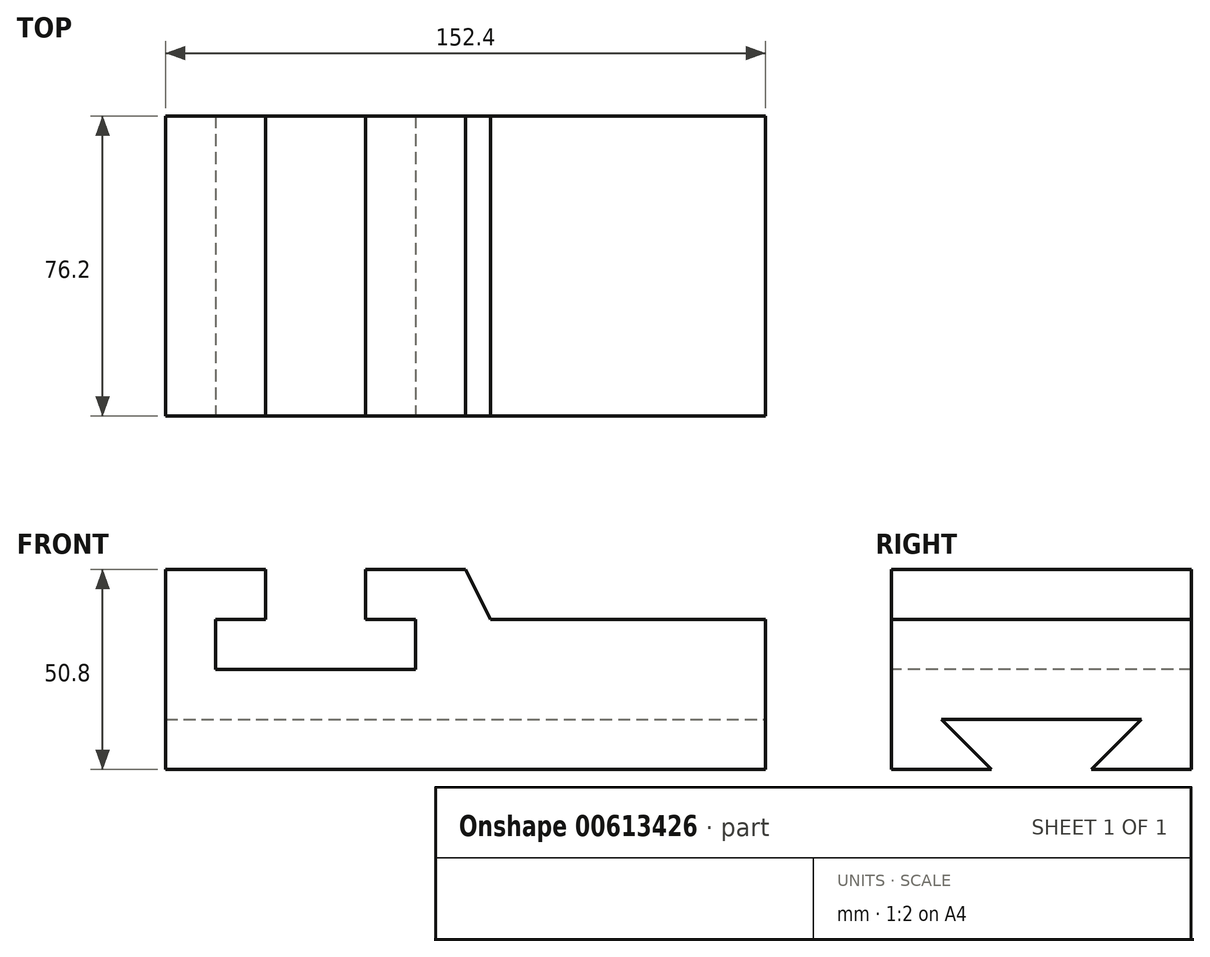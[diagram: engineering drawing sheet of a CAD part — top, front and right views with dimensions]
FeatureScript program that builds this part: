
annotation { "Feature Type Name" : "Feature", "Feature Type Description" : "" }
export const myFeature = defineFeature(function(context is Context, id is Id, definition is map)
    precondition{}
    {
        {
            var Q0;
            Q0=qCreatedBy(makeId("Front.planeOp"),FACE);
            var sketch = newSketch(context, id + "F0", { "sketchPlane" : qUnion([Q0])});
            skLineSegment(sketch, "E0.bottom", {"start": v(0, 0) * mm, "end": v(152.4, 0) * mm});
            skLineSegment(sketch, "E0.top", {"start": v(0, 50.8) * mm, "end": v(152.4, 50.8) * mm});
            skLineSegment(sketch, "E0.left", {"start": v(0, 0) * mm, "end": v(0, 50.8) * mm});
            skLineSegment(sketch, "E0.right", {"start": v(152.4, 0) * mm, "end": v(152.4, 50.8) * mm});
            skSolve(sketch);
        }
        {
            var Q0;
            Q0=makeQuery(id+"F0.imprint","IMPRINT",FACE,{"disambiguationData":[TD([[makeQuery(id+"F0.imprint","IMPRINT",EDGE,{"derivedFrom":sQuery(id+"F0.wireOp",EDGE,"E0.bottom")}),1.0]])]});
            extrude(context, id + "F1", {"entities" : qUnion([Q0]), "depth" : 76.2 * mm, "offsetDistance" : 25.4 * mm});
        }
        {
            var Q0;
            Q0=makeQuery(id+"F1.opExtrude","SWEPT_FACE",FACE,{"disambiguationData":[OSD([sQuery(id+"F0.wireOp",EDGE,"E0.right")])]});
            var sketch = newSketch(context, id + "F2", { "sketchPlane" : qUnion([Q0])});
            skLineSegment(sketch, "E1", {"start": v(-38.1, 0) * mm, "end": v(-25.4, 0) * mm});
            skLineSegment(sketch, "E2", {"start": v(-38.1, 0) * mm, "end": v(-50.8, 0) * mm});
            skLineSegment(sketch, "E3", {"start": v(-38.1, 12.7) * mm, "end": v(-12.7, 12.7) * mm});
            skLineSegment(sketch, "E4", {"start": v(-12.7, 12.7) * mm, "end": v(-25.4, 0) * mm});
            skLineSegment(sketch, "E5", {"start": v(-38.1, 12.7) * mm, "end": v(-63.5, 12.7) * mm});
            skLineSegment(sketch, "E6", {"start": v(-63.5, 12.7) * mm, "end": v(-50.8, 0) * mm});
            skSolve(sketch);
        }
        {
            var Q0;
            Q0 = qSketchRegion(id + "F2", true);
            extrude(context, id + "F3", {"entities" : qUnion([Q0]), "operationType" : NewBodyOperationType.REMOVE, "oppositeDirection" : true, "depth" : 152.4 * mm, "offsetDistance" : 25.4 * mm});
        }
        {
            var Q0;
            Q0=makeQuery(id+"F1.opExtrude","CAP_FACE",FACE,{"disambiguationData":[OSD([sQuery(id+"F0.wireOp",EDGE,"E0.bottom"),sQuery(id+"F0.wireOp",EDGE,"E0.top"),sQuery(id+"F0.wireOp",EDGE,"E0.left"),sQuery(id+"F0.wireOp",EDGE,"E0.right")])],"isStart":false});
            var sketch = newSketch(context, id + "F4", { "sketchPlane" : qUnion([Q0])});
            skLineSegment(sketch, "E7", {"start": v(0, 50.8) * mm, "end": v(25.4, 50.8) * mm});
            skLineSegment(sketch, "E8", {"start": v(25.4, 50.8) * mm, "end": v(25.4, 38.1) * mm});
            skLineSegment(sketch, "E9", {"start": v(25.4, 38.1) * mm, "end": v(12.7, 38.1) * mm});
            skLineSegment(sketch, "E10", {"start": v(12.7, 38.1) * mm, "end": v(12.7, 25.4) * mm});
            skLineSegment(sketch, "E11", {"start": v(12.7, 25.4) * mm, "end": v(63.5, 25.4) * mm});
            skLineSegment(sketch, "E12", {"start": v(63.5, 25.4) * mm, "end": v(63.5, 38.1) * mm});
            skLineSegment(sketch, "E13", {"start": v(63.5, 38.1) * mm, "end": v(50.8, 38.1) * mm});
            skLineSegment(sketch, "E14", {"start": v(50.8, 38.1) * mm, "end": v(50.8, 50.8) * mm});
            skSolve(sketch);
        }
        {
            var Q0;
            Q0 = qSketchRegion(id + "F4", true);
            var Q1;
            {var subQ0=sQuery(id+"F4.wireOp",EDGE,"E8");Q1=makeQuery(id+"F4.imprint","IMPRINT",FACE,{"disambiguationData":[TD([[makeQuery(id+"F4.imprint","IMPRINT",EDGE,{"derivedFrom":subQ0}),1.0]])]});}
            extrude(context, id + "F5", {"entities" : qUnion([Q0, Q1]), "operationType" : NewBodyOperationType.REMOVE, "oppositeDirection" : true, "depth" : 76.2 * mm, "offsetDistance" : 25.4 * mm});
        }
        {
            var Q0;
            Q0=makeQuery(id+"F1.opExtrude","CAP_FACE",FACE,{"disambiguationData":[OSD([sQuery(id+"F0.wireOp",EDGE,"E0.bottom"),sQuery(id+"F0.wireOp",EDGE,"E0.top"),sQuery(id+"F0.wireOp",EDGE,"E0.left"),sQuery(id+"F0.wireOp",EDGE,"E0.right")])],"isStart":false});
            var sketch = newSketch(context, id + "F6", { "sketchPlane" : qUnion([Q0])});
            skLineSegment(sketch, "E15", {"start": v(50.8, 50.8) * mm, "end": v(76.2, 50.8) * mm});
            skPoint(sketch, "E16.endSnap0", {"position": v(152.4, 25.4) * mm});
            skLineSegment(sketch, "E17", {"start": v(76.2, 50.8) * mm, "end": v(82.55, 38.1) * mm});
            skLineSegment(sketch, "E18", {"start": v(82.55, 38.1) * mm, "end": v(152.4, 38.1) * mm});
            skSolve(sketch);
        }
        {
            var Q0;
            Q0 = qSketchRegion(id + "F6", true);
            var Q1;
            {var subQ0=sQuery(id+"F6.wireOp",EDGE,"E17");Q1=makeQuery(id+"F6.imprint","IMPRINT",FACE,{"disambiguationData":[TD([[makeQuery(id+"F6.imprint","IMPRINT",EDGE,{"derivedFrom":subQ0}),1.0]])]});}
            extrude(context, id + "F7", {"entities" : qUnion([Q0, Q1]), "operationType" : NewBodyOperationType.REMOVE, "oppositeDirection" : true, "depth" : 76.2 * mm, "offsetDistance" : 25.4 * mm});
        }
    });
